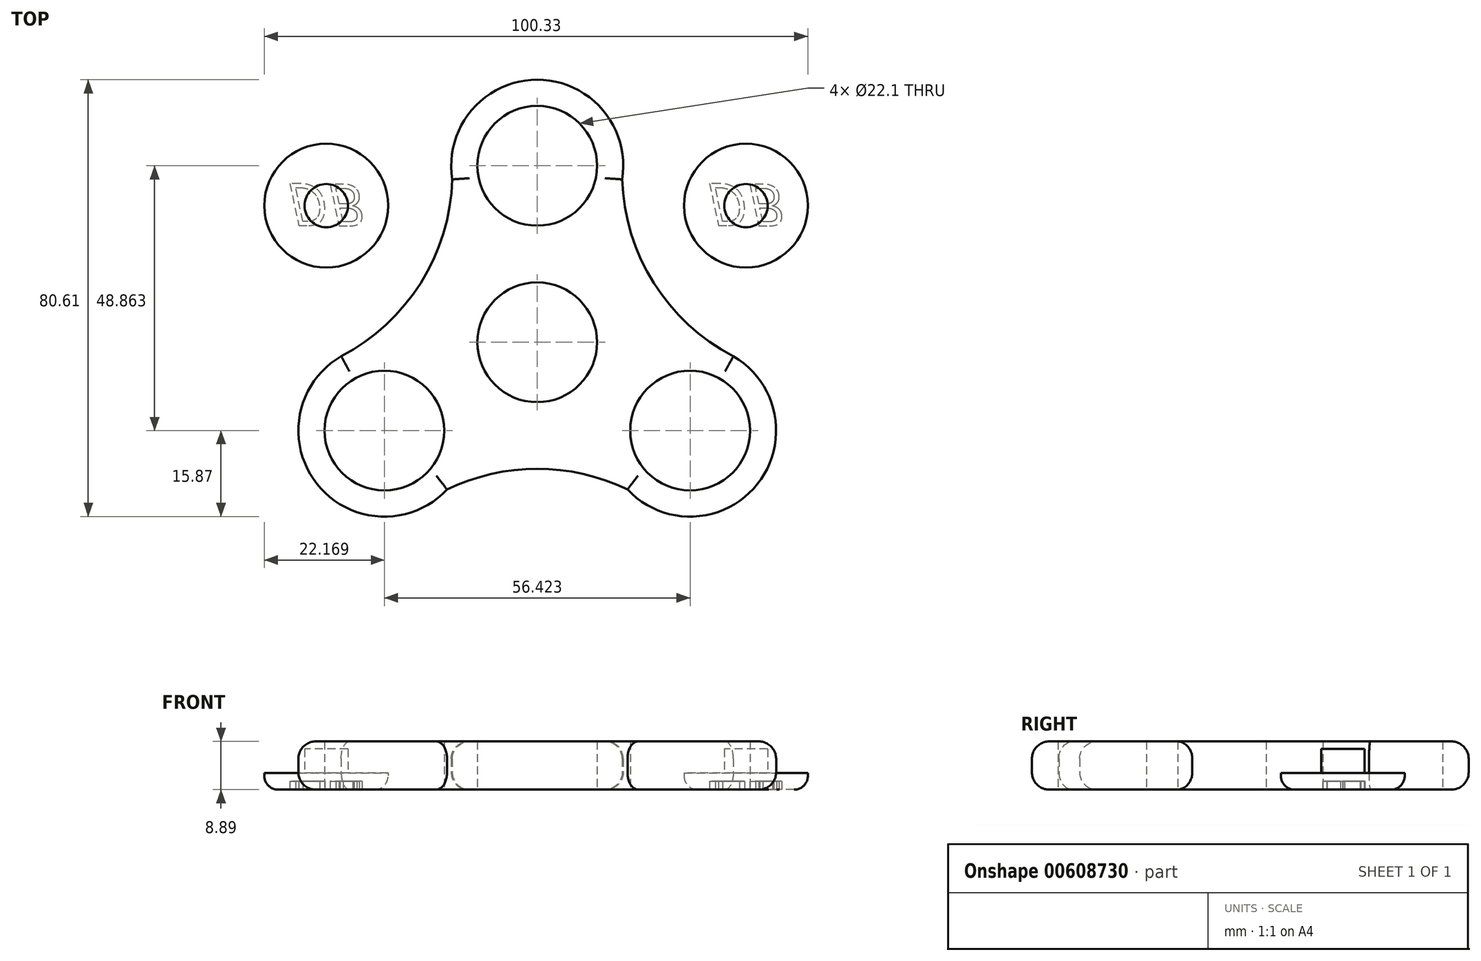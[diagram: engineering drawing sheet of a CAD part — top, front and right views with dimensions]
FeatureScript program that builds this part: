
annotation { "Feature Type Name" : "Feature", "Feature Type Description" : "" }
export const myFeature = defineFeature(function(context is Context, id is Id, definition is map)
    precondition{}
    {
        {
            var Q0;
            Q0=qCreatedBy(makeId("Top.planeOp"),FACE);
            var sketch = newSketch(context, id + "F0", { "sketchPlane" : qUnion([Q0])});
            skCircle(sketch, "E0", {"center": v(0, 59.75) * mm, "radius": 11.05 * mm});
            skCircle(sketch, "E1.1.0", {"center": v(-28.21, 10.9) * mm, "radius": 11.05 * mm});
            skCircle(sketch, "E1.2.0", {"center": v(28.21, 10.9) * mm, "radius": 11.05 * mm});
            skPoint(sketch, "E1.center", {"position": v(0, 27.18) * mm});
            skCircle(sketch, "E2", {"center": v(0, 27.18) * mm, "radius": 11.05 * mm});
            skArc(sketch, "E3", {"start": v(15.68, 57.25) * mm, "mid": v(0, 75.63) * mm, "end": v(-15.68, 57.25) * mm});
            skArc(sketch, "E4", {"start": v(-35.25, 25.12) * mm, "mid": v(-40.97, 1.45) * mm, "end": v(-16.66, 0) * mm});
            skArc(sketch, "E5", {"start": v(16.66, 0) * mm, "mid": v(40.97, 1.45) * mm, "end": v(35.25, 25.12) * mm});
            skArc(sketch, "E6", {"start": v(-36.2, 24.6) * mm, "mid": v(-21.5, 38.14) * mm, "end": v(-15.68, 57.25) * mm});
            skArc(sketch, "E7.MirrorCS", {"start": v(36.2, 24.6) * mm, "mid": v(21.5, 38.14) * mm, "end": v(15.68, 57.25) * mm});
            skArc(sketch, "E8", {"start": v(16.66, 0) * mm, "mid": v(0, 3.84) * mm, "end": v(-16.66, 0) * mm});
            skSolve(sketch);
        }
        {
            var Q0;
            Q0=makeQuery(id+"F0.imprint","IMPRINT",FACE,{"disambiguationData":[TD([[makeQuery(id+"F0.imprint","IMPRINT",EDGE,{"derivedFrom":sQuery(id+"F0.wireOp",EDGE,"E0")}),-1.0]])]});
            extrude(context, id + "F1", {"entities" : qUnion([Q0]), "depth" : 8.9 * mm, "offsetDistance" : 25.4 * mm});
        }
        {
            var Q0;
            Q0=makeQuery(id+"F1.opExtrude","CAP_EDGE",EDGE,{"disambiguationData":[OSD([sQuery(id+"F0.wireOp",EDGE,"E4")])],"isStart":false});
            var Q1;
            Q1=makeQuery(id+"F1.opExtrude","CAP_EDGE",EDGE,{"disambiguationData":[OSD([sQuery(id+"F0.wireOp",EDGE,"E8")])],"isStart":false});
            var Q2;
            Q2=makeQuery(id+"F1.opExtrude","CAP_EDGE",EDGE,{"disambiguationData":[OSD([sQuery(id+"F0.wireOp",EDGE,"E5")])],"isStart":false});
            var Q3;
            Q3=makeQuery(id+"F1.opExtrude","CAP_EDGE",EDGE,{"disambiguationData":[OSD([sQuery(id+"F0.wireOp",EDGE,"E7.MirrorCS")])],"isStart":false});
            var Q4;
            Q4=makeQuery(id+"F1.opExtrude","CAP_EDGE",EDGE,{"disambiguationData":[OSD([sQuery(id+"F0.wireOp",EDGE,"E3")])],"isStart":false});
            var Q5;
            Q5=makeQuery(id+"F1.opExtrude","CAP_EDGE",EDGE,{"disambiguationData":[OSD([sQuery(id+"F0.wireOp",EDGE,"E6")])],"isStart":false});
            var Q6;
            Q6=makeQuery(id+"F1.opExtrude","CAP_EDGE",EDGE,{"disambiguationData":[OSD([sQuery(id+"F0.wireOp",EDGE,"E6")])],"isStart":true});
            var Q7;
            Q7=makeQuery(id+"F1.opExtrude","CAP_EDGE",EDGE,{"disambiguationData":[OSD([sQuery(id+"F0.wireOp",EDGE,"E3")])],"isStart":true});
            var Q8;
            Q8=makeQuery(id+"F1.opExtrude","CAP_EDGE",EDGE,{"disambiguationData":[OSD([sQuery(id+"F0.wireOp",EDGE,"E7.MirrorCS")])],"isStart":true});
            var Q9;
            Q9=makeQuery(id+"F1.opExtrude","CAP_EDGE",EDGE,{"disambiguationData":[OSD([sQuery(id+"F0.wireOp",EDGE,"E5")])],"isStart":true});
            var Q10;
            Q10=makeQuery(id+"F1.opExtrude","CAP_EDGE",EDGE,{"disambiguationData":[OSD([sQuery(id+"F0.wireOp",EDGE,"E8")])],"isStart":true});
            var Q11;
            Q11=makeQuery(id+"F1.opExtrude","CAP_EDGE",EDGE,{"disambiguationData":[OSD([sQuery(id+"F0.wireOp",EDGE,"E4")])],"isStart":true});
            fillet(context, id + "F2", {"entities" : qUnion([Q0, Q1, Q2, Q3, Q4, Q5, Q6, Q7, Q8, Q9, Q10, Q11]), "radius" : 3.17 * mm, "tangentPropagation" : true, "allowEdgeOverflow" : false});
        }
        {
            var Q0;
            Q0=qCreatedBy(makeId("Top.planeOp"),FACE);
            var sketch = newSketch(context, id + "F3", { "sketchPlane" : qUnion([Q0])});
            skCircle(sketch, "E9", {"center": v(38.52, 52.4) * mm, "radius": 11.43 * mm});
            skSolve(sketch);
        }
        {
            var Q0;
            Q0=makeQuery(id+"F3.imprint","IMPRINT",FACE,{"disambiguationData":[TD([[makeQuery(id+"F3.imprint","IMPRINT",EDGE,{"derivedFrom":sQuery(id+"F3.wireOp",EDGE,"E9")}),1.0]])]});
            extrude(context, id + "F4", {"entities" : qUnion([Q0]), "depth" : 3.05 * mm, "offsetDistance" : 25.4 * mm});
        }
        {
            var Q0;
            Q0=makeQuery(id+"F4.opExtrude","CAP_FACE",FACE,{"disambiguationData":[OSD([sQuery(id+"F3.wireOp",EDGE,"E9")])],"isStart":false});
            var sketch = newSketch(context, id + "F5", { "sketchPlane" : qUnion([Q0])});
            skCircle(sketch, "E10", {"center": v(38.52, 52.4) * mm, "radius": 4 * mm});
            skSolve(sketch);
        }
        {
            var Q0;
            Q0=makeQuery(id+"F5.imprint","IMPRINT",FACE,{"disambiguationData":[TD([[makeQuery(id+"F5.imprint","IMPRINT",EDGE,{"derivedFrom":sQuery(id+"F5.wireOp",EDGE,"E10")}),1.0]])]});
            extrude(context, id + "F6", {"entities" : qUnion([Q0]), "operationType" : NewBodyOperationType.ADD, "depth" : 4.44 * mm, "offsetDistance" : 25.4 * mm});
        }
        {
            var Q0;
            Q0=makeQuery(id+"F4.opExtrude","CAP_EDGE",EDGE,{"disambiguationData":[OSD([sQuery(id+"F3.wireOp",EDGE,"E9")])],"isStart":true});
            fillet(context, id + "F7", {"entities" : qUnion([Q0]), "radius" : 2.54 * mm, "tangentPropagation" : true, "allowEdgeOverflow" : false});
        }
        {
            var Q0;
            Q0=makeQuery(id+"F4.opExtrude","CAP_FACE",FACE,{"disambiguationData":[OSD([sQuery(id+"F3.wireOp",EDGE,"E9")])],"isStart":true});
            var sketch = newSketch(context, id + "F8", { "sketchPlane" : qUnion([Q0])});
            skText(sketch, "E11", { "text": "B", "fontName": "OpenSans-Italic.ttf"});
            const initialGuessF8  = {"E11": [0.0388, -0.05636, 1, 0, 0.00778]};
            skSetInitialGuess(sketch, initialGuessF8);
            skSolve(sketch);
        }
        {
            var Q0;
            Q0 = qSketchRegion(id + "F8", true);
            extrude(context, id + "F9", {"entities" : qUnion([Q0]), "operationType" : NewBodyOperationType.REMOVE, "oppositeDirection" : true, "depth" : 1.52 * mm, "offsetDistance" : 25.4 * mm});
        }
        {
            var Q0;
            {var subQ0=sQuery(id+"F3.wireOp",EDGE,"E9");Q0=makeQuery(id+"F9.boolean.opBoolean","SPLIT",FACE,{"disambiguationData":[TD([makeQuery(id+"F7.opFillet","BLEND_FACE",FACE,{"disambiguationData":[OSD([subQ0])]})])],"derivedFrom":makeQuery(id+"F4.opExtrude","CAP_FACE",FACE,{"disambiguationData":[OSD([subQ0])],"isStart":true})});}
            var sketch = newSketch(context, id + "F10", { "sketchPlane" : qUnion([Q0])});
            skText(sketch, "E12", { "text": "D", "fontName": "OpenSans-Italic.ttf"});
            const initialGuessF10  = {"E12": [0.03135, -0.05649, 1, 0, 0.00783]};
            skSetInitialGuess(sketch, initialGuessF10);
            skSolve(sketch);
        }
        {
            var Q0;
            Q0=makeQuery(id+"F10.imprint","IMPRINT",FACE,{"disambiguationData":[TD([[makeQuery(id+"F10.imprint","IMPRINT",EDGE,{"derivedFrom":sQuery(id+"F10.wireOp",EDGE,"E12.sketch_text.stroke-0")}),-1.0]])]});
            extrude(context, id + "F11", {"entities" : qUnion([Q0]), "operationType" : NewBodyOperationType.REMOVE, "oppositeDirection" : true, "depth" : 1.52 * mm, "offsetDistance" : 25.4 * mm});
        }
        {
            var Q0;
            Q0=makeQuery(id+"F4.opExtrude","SWEPT_BODY",BODY,{"disambiguationData":[OSD([sQuery(id+"F3.wireOp",EDGE,"E9")])]});
            transform(context, id + "F12", {"entities" : qUnion([Q0]), "transformType" : TransformType.TRANSLATION_3D, "dx" : -77.47 * mm, "dy" : 0 * mm, "dz" : 0 * mm, "makeCopy" : true});
        }
    });
